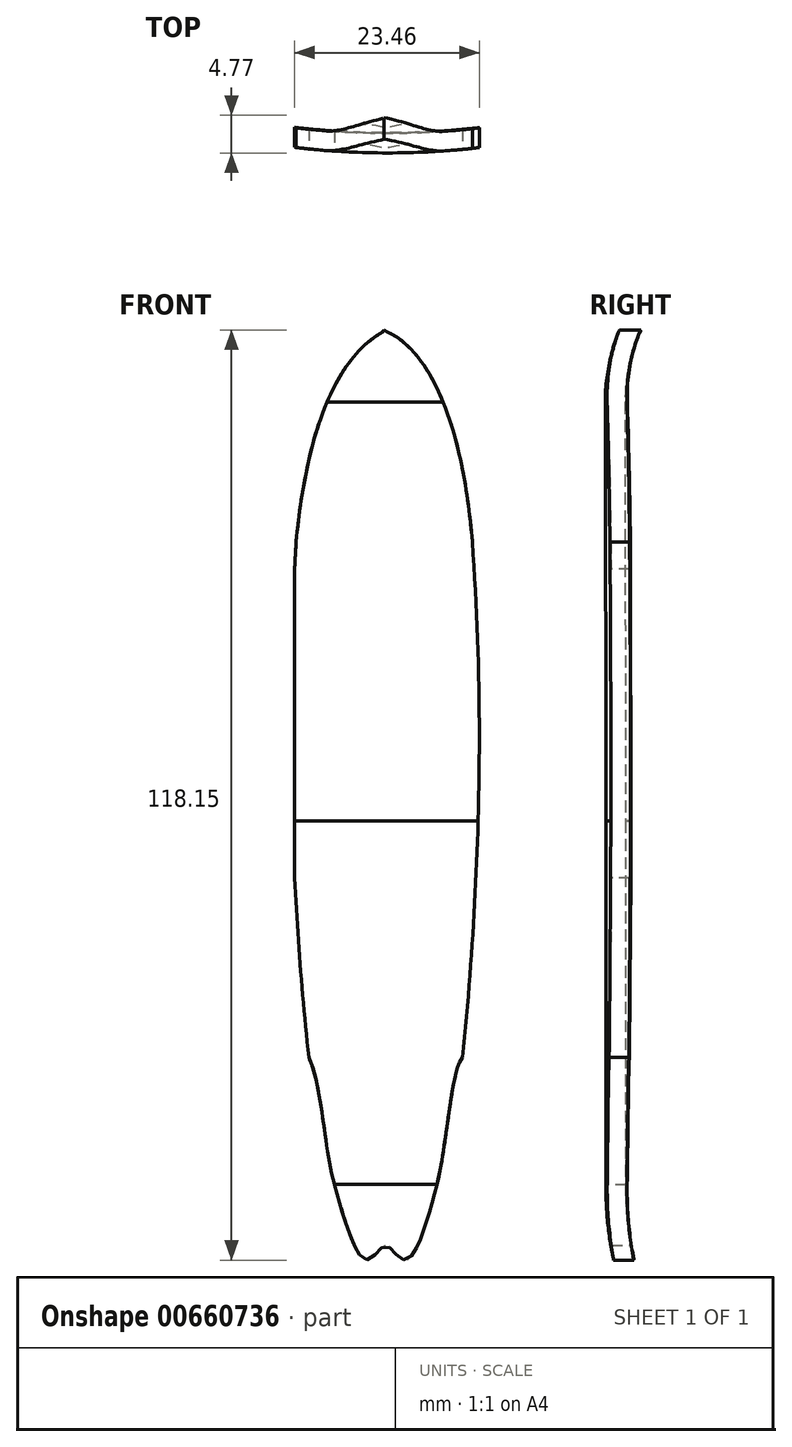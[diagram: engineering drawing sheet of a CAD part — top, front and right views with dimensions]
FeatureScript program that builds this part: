
annotation { "Feature Type Name" : "Feature", "Feature Type Description" : "" }
export const myFeature = defineFeature(function(context is Context, id is Id, definition is map)
    precondition{}
    {
        {
            var Q0;
            Q0=qCreatedBy(makeId("Front.planeOp"),FACE);
            var sketch = newSketch(context, id + "F0", { "sketchPlane" : qUnion([Q0])});
            skPoint(sketch, "E0.0.internal.snap0", {"position": v(-0.51, 63.2) * mm});
            skFitSpline(sketch, "E0", {"points": [v(-0.51, 62.37) * mm, v(-11.68, 35.47) * mm], "startDerivative": vector(0.54, -2.11) * mm, "endDerivative": vector(-7.05, -74.64) * mm});
            skFitSpline(sketch, "E1", {"points": [v(-0.51, 62.37) * mm, v(10.7, 35.47) * mm], "startDerivative": vector(0.54, -0.94) * mm, "endDerivative": vector(6.26, -74.64) * mm});
            skFitSpline(sketch, "E2", {"points": [v(-11.68, 35.47) * mm, v(-10.07, -30.04) * mm], "startDerivative": vector(-4, -67.06) * mm, "endDerivative": vector(6.86, -63.66) * mm});
            skFitSpline(sketch, "E3", {"points": [v(10.7, 35.47) * mm, v(9.47, -30.04) * mm], "startDerivative": vector(4.9, -67.06) * mm, "endDerivative": vector(-6.36, -63.66) * mm});
            skFitSpline(sketch, "E4", {"points": [v(-10.07, -30.04) * mm, v(-6.8, -46.2) * mm], "startDerivative": vector(5.38, -12.23) * mm, "endDerivative": vector(4.1, -14.18) * mm});
            skFitSpline(sketch, "E5", {"points": [v(9.47, -30.04) * mm, v(6.2, -46.2) * mm], "startDerivative": vector(-4.57, -5.2) * mm, "endDerivative": vector(-4.1, -16.37) * mm});
            skFitSpline(sketch, "E6", {"points": [v(-6.8, -46.2) * mm, v(-4.44, -53.56) * mm, v(-3.69, -54.98) * mm, v(-2.9, -55.74) * mm, v(-1.42, -54.9) * mm, v(-0.32, -53.9) * mm, v(0.82, -54.86) * mm, v(2.39, -55.77) * mm, v(3.3, -54.75) * mm, v(4.1, -53.18) * mm, v(6.2, -46.2) * mm], "startDerivative": vector(11.6, -45.36) * mm, "endDerivative": vector(11.28, 45.7) * mm});
            skLineSegment(sketch, "E7.bottom", {"start": v(37.9, 73.92) * mm, "end": v(-52.4, 73.92) * mm});
            skLineSegment(sketch, "E7.top", {"start": v(37.9, -69.75) * mm, "end": v(-52.4, -69.75) * mm});
            skLineSegment(sketch, "E7.left", {"start": v(37.9, 73.92) * mm, "end": v(37.9, -69.75) * mm});
            skLineSegment(sketch, "E7.right", {"start": v(-52.4, 73.92) * mm, "end": v(-52.4, -69.75) * mm});
            skSolve(sketch);
        }
        {
            var Q0;
            Q0=qCreatedBy(makeId("Top.planeOp"),FACE);
            var sketch = newSketch(context, id + "F1", { "sketchPlane" : qUnion([Q0])});
            skArc(sketch, "E8", {"start": v(-11.87, 5.22) * mm, "mid": v(0, 4.53) * mm, "end": v(11.87, 5.22) * mm});
            skLineSegment(sketch, "E9", {"start": v(-11.87, 5.22) * mm, "end": v(-11.87, 2.72) * mm});
            skLineSegment(sketch, "E10", {"start": v(11.87, 5.22) * mm, "end": v(11.87, 2.72) * mm});
            skArc(sketch, "E11", {"start": v(-11.87, 2.72) * mm, "mid": v(0, 2.03) * mm, "end": v(11.87, 2.72) * mm});
            skLineSegment(sketch, "E12", {"start": v(-11.87, 5.22) * mm, "end": v(0, 5.22) * mm, "construction": true});
            skLineSegment(sketch, "E13", {"start": v(0, 5.22) * mm, "end": v(11.87, 5.22) * mm, "construction": true});
            skSolve(sketch);
        }
        {
            var Q0;
            Q0=qCreatedBy(makeId("Right.planeOp"),FACE);
            var sketch = newSketch(context, id + "F2", { "sketchPlane" : qUnion([Q0])});
            skLineSegment(sketch, "E14", {"start": v(0, 63.14) * mm, "end": v(4.88, 63.14) * mm, "construction": true});
            skLineSegment(sketch, "E15", {"start": v(0, -46.14) * mm, "end": v(5.13, -46.14) * mm, "construction": true});
            skLineSegment(sketch, "E16", {"start": v(2.93, 0) * mm, "end": v(2.93, -46.14) * mm});
            skLineSegment(sketch, "E17", {"start": v(0, -56.84) * mm, "end": v(5.4, -56.84) * mm, "construction": true});
            skArc(sketch, "E18", {"start": v(2.93, -46.14) * mm, "mid": v(3.24, -51.53) * mm, "end": v(4.18, -56.84) * mm});
            skLineSegment(sketch, "E19", {"start": v(0, 50.63) * mm, "end": v(2.88, 50.63) * mm, "construction": true});
            skLineSegment(sketch, "E20", {"start": v(2.93, 0) * mm, "end": v(2.88, 53.21) * mm});
            skArc(sketch, "E21", {"start": v(5.07, 63.14) * mm, "mid": v(3.43, 58.3) * mm, "end": v(2.88, 53.21) * mm});
            skSolve(sketch);
        }
        {
            var Q0;
            Q0=makeQuery(id+"F1.imprint","IMPRINT",FACE,{"disambiguationData":[TD([[makeQuery(id+"F1.imprint","IMPRINT",EDGE,{"derivedFrom":sQuery(id+"F1.wireOp",EDGE,"E8")}),-1.0]])]});
            var Q1;
            Q1=sQuery(id+"F2.wireOp",EDGE,"E20");
            var Q2;
            Q2=sQuery(id+"F2.wireOp",EDGE,"E21");
            var Q3;
            Q3=sQuery(id+"F2.wireOp",EDGE,"E16");
            var Q4;
            Q4=sQuery(id+"F2.wireOp",EDGE,"E18");
            sweep(context, id + "F3", {"profiles" : qUnion([Q0]), "path" : qUnion([Q1, Q2, Q3, Q4])});
        }
        {
            var Q0;
            Q0 = qSketchRegion(id + "F0", true);
            extrude(context, id + "F4", {"entities" : qUnion([Q0]), "operationType" : NewBodyOperationType.REMOVE, "oppositeDirection" : true, "depth" : 25 * mm, "offsetDistance" : 25 * mm});
        }
        {
            var Q0;
            Q0=makeQuery(id+"F3.opSweep","MID_CAP_VERTEX",VERTEX,{"disambiguationData":[OSD([sQuery(id+"F1.wireOp",EDGE,"E9"),sQuery(id+"F1.wireOp",EDGE,"E11"),sQuery(id+"F2.wireOp",EDGE,"E16")])],"capPos":2.0});
            var Q1;
            {var subQ0=sQuery(id+"F1.wireOp",EDGE,"E11");Q1=makeQuery(id+"F4.boolean.opBoolean","INTERSECT",VERTEX,{"derivedFrom":[makeQuery(id+"F3.opSweep","SWEPT_FACE",FACE,{"disambiguationData":[OSD([subQ0,sQuery(id+"F2.wireOp",EDGE,"E16")])]}),makeQuery(id+"F3.opSweep","SWEPT_FACE",FACE,{"disambiguationData":[OSD([subQ0,sQuery(id+"F2.wireOp",EDGE,"E20")])]}),makeQuery(id+"F4.opExtrude","SWEPT_FACE",FACE,{"disambiguationData":[OSD([sQuery(id+"F0.wireOp",EDGE,"E3")])]})]});}
            var Q2;
            {var subQ0=sQuery(id+"F1.wireOp",EDGE,"E11");Q2=makeQuery(id+"F4.boolean.opBoolean","INTERSECT",VERTEX,{"derivedFrom":[makeQuery(id+"F3.opSweep","SWEPT_FACE",FACE,{"disambiguationData":[OSD([subQ0,sQuery(id+"F2.wireOp",EDGE,"E16")])]}),makeQuery(id+"F3.opSweep","SWEPT_FACE",FACE,{"disambiguationData":[OSD([subQ0,sQuery(id+"F2.wireOp",EDGE,"E18")])]}),makeQuery(id+"F4.opExtrude","SWEPT_FACE",FACE,{"disambiguationData":[OSD([sQuery(id+"F0.wireOp",EDGE,"E4")])]})]});}
            cPlane(context, id + "F5", {"entities" : qUnion([Q0, Q1, Q2]), "cplaneType" : CPlaneType.THREE_POINT, "offset" : 25 * mm, "width" : 150 * mm, "height" : 150 * mm});
        }
    });
